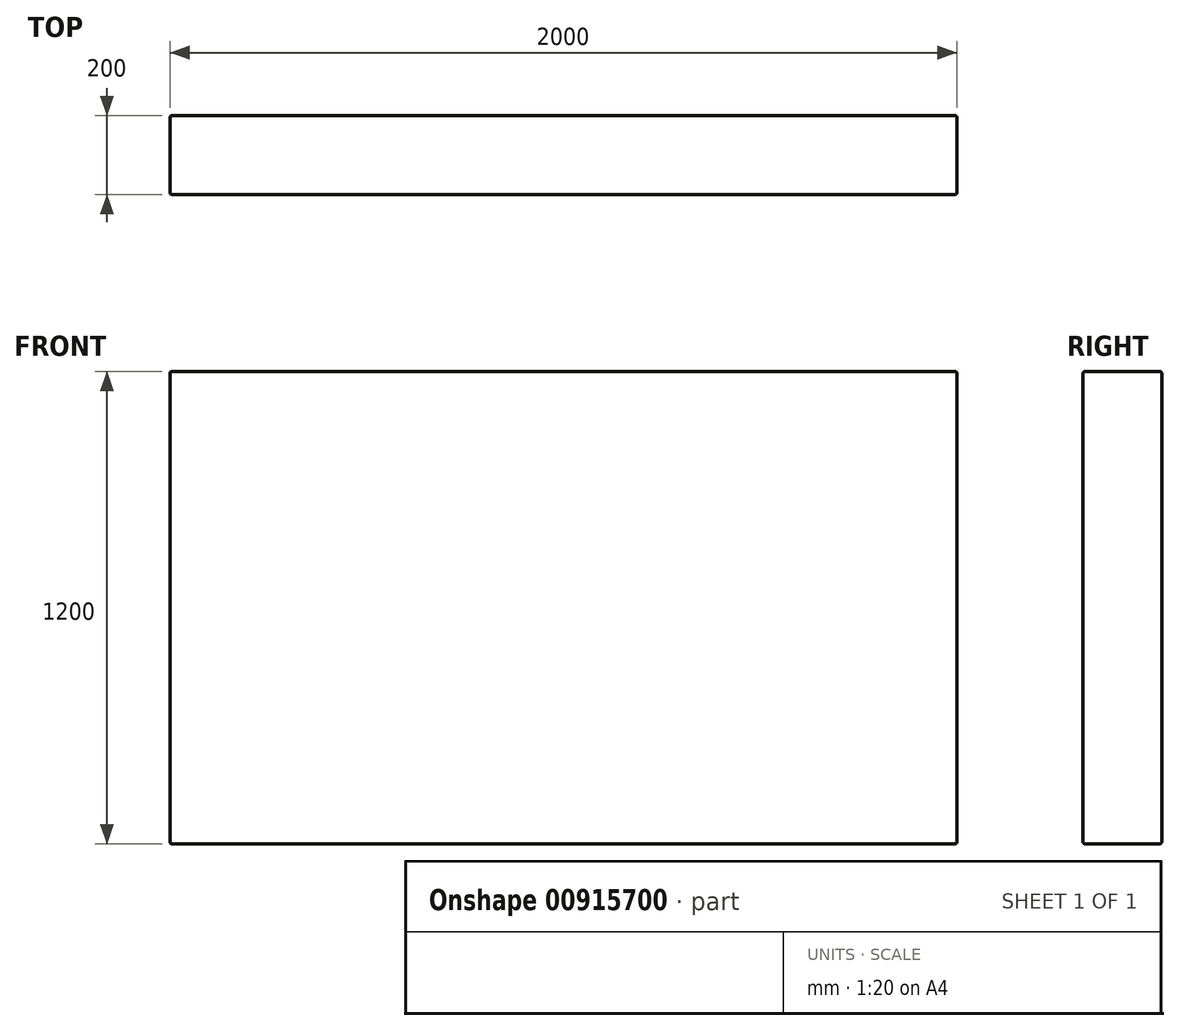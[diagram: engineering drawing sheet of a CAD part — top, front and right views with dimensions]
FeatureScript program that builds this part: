
annotation { "Feature Type Name" : "Feature", "Feature Type Description" : "" }
export const myFeature = defineFeature(function(context is Context, id is Id, definition is map)
    precondition{}
    {
        {
            var Q0;
            Q0=qCreatedBy(makeId("Front.planeOp"),FACE);
            var sketch = newSketch(context, id + "F0", { "sketchPlane" : qUnion([Q0])});
            skLineSegment(sketch, "E0", {"start": v(-205.54, 0) * mm, "end": v(1794.46, 0) * mm});
            skLineSegment(sketch, "E1", {"start": v(1794.46, 0) * mm, "end": v(1794.46, 1200) * mm});
            skLineSegment(sketch, "E2", {"start": v(1794.46, 1200) * mm, "end": v(-205.54, 1200) * mm});
            skLineSegment(sketch, "E3", {"start": v(-205.54, 1200) * mm, "end": v(-205.54, 0) * mm});
            skSolve(sketch);
        }
        {
            var Q0;
            Q0 = qSketchRegion(id + "F0", true);
            extrude(context, id + "F1", {"entities" : qUnion([Q0]), "depth" : 25 * mm, "offsetDistance" : 25 * mm});
        }
        {
            var Q0;
            Q0 = qSketchRegion(id + "F0", true);
            extrude(context, id + "F2", {"entities" : qUnion([Q0]), "operationType" : NewBodyOperationType.ADD, "depth" : 200 * mm, "offsetDistance" : 25 * mm});
        }
        {
            var Q0;
            Q0=makeQuery(id+"F2.opExtrude","CAP_EDGE",EDGE,{"disambiguationData":[OSD([sQuery(id+"F0.wireOp",EDGE,"E2")])],"isStart":false});
            var Q1;
            Q1=makeQuery(id+"F2.opExtrude","CAP_FACE",FACE,{"disambiguationData":[OSD([sQuery(id+"F0.wireOp",EDGE,"E0"),sQuery(id+"F0.wireOp",EDGE,"E1"),sQuery(id+"F0.wireOp",EDGE,"E2"),sQuery(id+"F0.wireOp",EDGE,"E3")])],"isStart":false});
            var Q2;
            {var subQ0=sQuery(id+"F0.wireOp",EDGE,"E0");Q2=makeQuery(id+"F2.boolean.opBoolean","MERGE",FACE,{"derivedFrom":[makeQuery(id+"F1.opExtrude","SWEPT_FACE",FACE,{"disambiguationData":[OSD([subQ0])]}),makeQuery(id+"F2.opExtrude","SWEPT_FACE",FACE,{"disambiguationData":[OSD([subQ0])]})]});}
            var Q3;
            {var subQ0=sQuery(id+"F0.wireOp",EDGE,"E1");Q3=makeQuery(id+"F2.boolean.opBoolean","MERGE",FACE,{"derivedFrom":[makeQuery(id+"F1.opExtrude","SWEPT_FACE",FACE,{"disambiguationData":[OSD([subQ0])]}),makeQuery(id+"F2.opExtrude","SWEPT_FACE",FACE,{"disambiguationData":[OSD([subQ0])]})]});}
            var Q4;
            Q4=makeQuery(id+"F1.opExtrude","CAP_FACE",FACE,{"disambiguationData":[OSD([sQuery(id+"F0.wireOp",EDGE,"E0"),sQuery(id+"F0.wireOp",EDGE,"E1"),sQuery(id+"F0.wireOp",EDGE,"E2"),sQuery(id+"F0.wireOp",EDGE,"E3")])],"isStart":true});
            var Q5;
            {var subQ0=sQuery(id+"F0.wireOp",EDGE,"E3");Q5=makeQuery(id+"F2.boolean.opBoolean","MERGE",FACE,{"derivedFrom":[makeQuery(id+"F1.opExtrude","SWEPT_FACE",FACE,{"disambiguationData":[OSD([subQ0])]}),makeQuery(id+"F2.opExtrude","SWEPT_FACE",FACE,{"disambiguationData":[OSD([subQ0])]})]});}
            fillet(context, id + "F3", {"entities" : qUnion([Q0, Q1, Q2, Q3, Q4, Q5]), "radius" : 5 * mm, "tangentPropagation" : true, "allowEdgeOverflow" : false});
        }
    });
